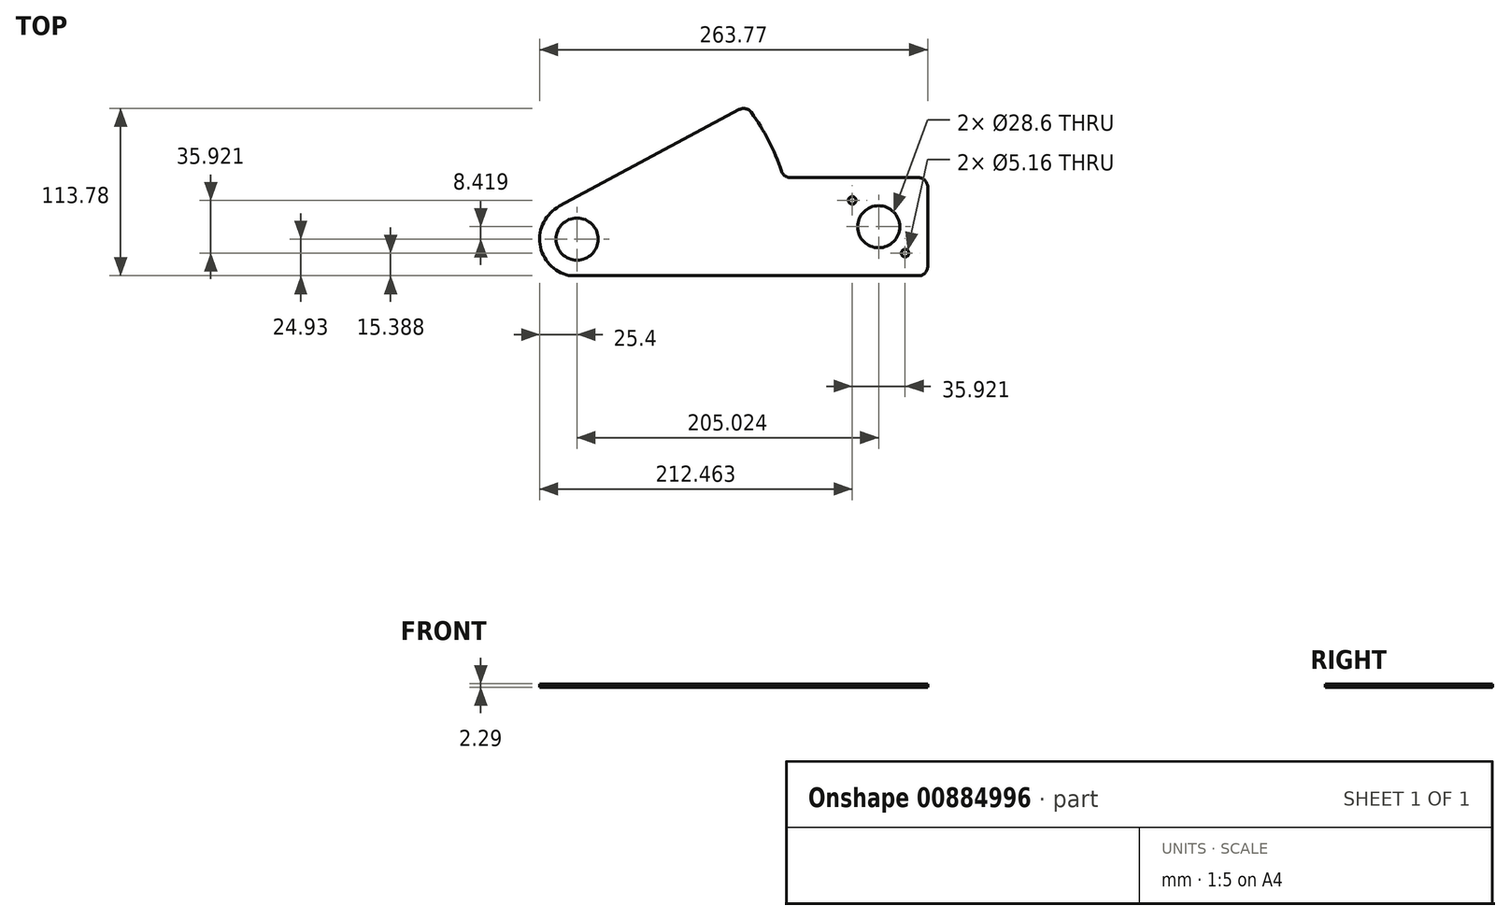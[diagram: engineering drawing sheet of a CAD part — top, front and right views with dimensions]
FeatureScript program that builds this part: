
annotation { "Feature Type Name" : "Feature", "Feature Type Description" : "" }
export const myFeature = defineFeature(function(context is Context, id is Id, definition is map)
    precondition{}
    {
        {
            var Q0;
            Q0=qCreatedBy(makeId("Top.planeOp"),FACE);
            var sketch = newSketch(context, id + "F0", { "sketchPlane" : qUnion([Q0])});
            skCircle(sketch, "E0", {"center": v(0, 0) * mm, "radius": 14.3 * mm});
            skArc(sketch, "E1", {"start": v(5.6, -24.78) * mm, "mid": v(0, 25.4) * mm, "end": v(-5.6, -24.78) * mm});
            skArc(sketch, "E2", {"start": v(139.02, 46.12) * mm, "mid": v(130.26, 66.98) * mm, "end": v(118.4, 86.24) * mm});
            skLineSegment(sketch, "E3", {"start": v(110.25, 88.1) * mm, "end": v(-12.03, 22.37) * mm});
            skPoint(sketch, "E4.visualSharp", {"position": v(168.28, -25.4) * mm});
            skPoint(sketch, "E5.visualSharp", {"position": v(115.04, 90.67) * mm});
            skArc(sketch, "E5.filletArc", {"start": v(118.4, 86.24) * mm, "mid": v(114.67, 88.7) * mm, "end": v(110.25, 88.1) * mm});
            skArc(sketch, "E6", {"start": v(155.58, 0) * mm, "mid": v(144.39, 57.93) * mm, "end": v(112.43, 107.53) * mm});
            skCircle(sketch, "E7", {"center": v(205.02, 8.42) * mm, "radius": 14.3 * mm});
            skLineSegment(sketch, "E8", {"start": v(145.05, 41.77) * mm, "end": v(232.02, 41.77) * mm});
            skLineSegment(sketch, "E9", {"start": v(238.37, 35.42) * mm, "end": v(238.37, -18.58) * mm});
            skPoint(sketch, "E10.visualSharp", {"position": v(-25.4, -25.4) * mm});
            skPoint(sketch, "E11.visualSharp", {"position": v(238.37, -24.93) * mm});
            skPoint(sketch, "E12.visualSharp", {"position": v(238.37, 41.77) * mm});
            skArc(sketch, "E12.filletArc", {"start": v(238.37, 35.42) * mm, "mid": v(236.51, 39.9) * mm, "end": v(232.02, 41.77) * mm});
            skArc(sketch, "E13.filletArc", {"start": v(139.02, 46.12) * mm, "mid": v(141.33, 42.97) * mm, "end": v(145.05, 41.77) * mm});
            skPoint(sketch, "E14.start.orphan", {"position": v(-25.4, 0) * mm});
            skPoint(sketch, "E15.orphan", {"position": v(238.37, -18.58) * mm});
            skCircle(sketch, "E16", {"center": v(187.06, 26.38) * mm, "radius": 2.58 * mm});
            skCircle(sketch, "E17", {"center": v(222.98, -9.54) * mm, "radius": 2.58 * mm});
            skPoint(sketch, "E18.orphan", {"position": v(187.06, 8.42) * mm});
            skPoint(sketch, "E19.end.orphan", {"position": v(222.98, 8.42) * mm});
            skLineSegment(sketch, "E20", {"start": v(161.95, -24.93) * mm, "end": v(232.02, -24.93) * mm});
            skLineSegment(sketch, "E21", {"start": v(238.37, -18.58) * mm, "end": v(238.37, -18.58) * mm});
            skLineSegment(sketch, "E22", {"start": v(161.95, -24.93) * mm, "end": v(159.66, -24.92) * mm});
            skLineSegment(sketch, "E23", {"start": v(205.02, 8.42) * mm, "end": v(222.98, -9.54) * mm});
            skLineSegment(sketch, "E24", {"start": v(187.06, 26.38) * mm, "end": v(205.02, 8.42) * mm});
            skArc(sketch, "E25.filletArc", {"start": v(232.02, -24.93) * mm, "mid": v(236.51, -23.07) * mm, "end": v(238.37, -18.58) * mm});
            skLineSegment(sketch, "E26", {"start": v(4.2, -24.93) * mm, "end": v(-4.2, -24.93) * mm});
            skPoint(sketch, "E27.visualSharp", {"position": v(-4.86, -24.93) * mm});
            skArc(sketch, "E27.filletArc", {"start": v(-5.6, -24.78) * mm, "mid": v(-4.9, -24.9) * mm, "end": v(-4.2, -24.93) * mm});
            skPoint(sketch, "E28.visualSharp", {"position": v(4.86, -24.93) * mm});
            skArc(sketch, "E28.filletArc", {"start": v(4.2, -24.93) * mm, "mid": v(4.9, -24.9) * mm, "end": v(5.6, -24.78) * mm});
            skLineSegment(sketch, "E29", {"start": v(159.66, -24.92) * mm, "end": v(4.58, -24.92) * mm});
            skSolve(sketch);
        }
        {
            var Q0;
            Q0 = qSketchRegion(id + "F0", true);
            extrude(context, id + "F1", {"entities" : qUnion([Q0]), "depth" : 2.3 * mm, "offsetDistance" : 25.4 * mm});
        }
    });
